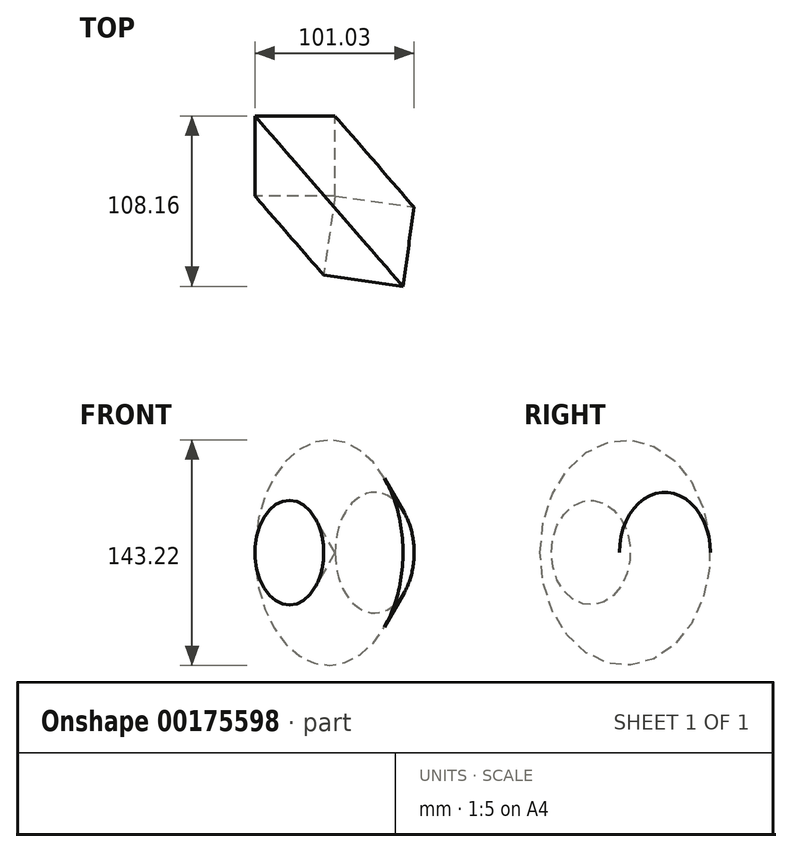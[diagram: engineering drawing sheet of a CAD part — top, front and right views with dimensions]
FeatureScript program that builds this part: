
annotation { "Feature Type Name" : "Feature", "Feature Type Description" : "" }
export const myFeature = defineFeature(function(context is Context, id is Id, definition is map)
    precondition{}
    {
        {
            var Q0;
            Q0=qCreatedBy(makeId("Top.planeOp"),FACE);
            var sketch = newSketch(context, id + "F0", { "sketchPlane" : qUnion([Q0])});
            skLineSegment(sketch, "E0.bottom", {"start": v(0, 0) * mm, "end": v(-50.8, 0) * mm});
            skLineSegment(sketch, "E0.top", {"start": v(0, 50.8) * mm, "end": v(-50.8, 50.8) * mm});
            skLineSegment(sketch, "E0.left", {"start": v(0, 0) * mm, "end": v(0, 50.8) * mm});
            skLineSegment(sketch, "E0.right", {"start": v(-50.8, 0) * mm, "end": v(-50.8, 50.8) * mm});
            skLineSegment(sketch, "E1", {"start": v(0, 0) * mm, "end": v(-26.53, -22.96) * mm});
            skLineSegment(sketch, "E2", {"start": v(-26.53, -22.96) * mm, "end": v(25.39, 22.1) * mm});
            skSolve(sketch);
        }
        {
            var Q0;
            {var subQ2=sQuery(id+"F0.wireOp",EDGE,"E0.top");Q0=makeQuery(id+"F0.imprint","IMPRINT",FACE,{"disambiguationData":[TD([[makeQuery(id+"F0.imprint","IMPRINT",EDGE,{"derivedFrom":subQ2}),1.0]])]});}
            var Q1;
            Q1=sQuery(id+"F0.wireOp",EDGE,"E2");
            revolve(context, id + "F1", {"entities" : qUnion([Q0]), "axis" : qUnion([Q1]), "revolveType" : RevolveType.FULL});
        }
    });
